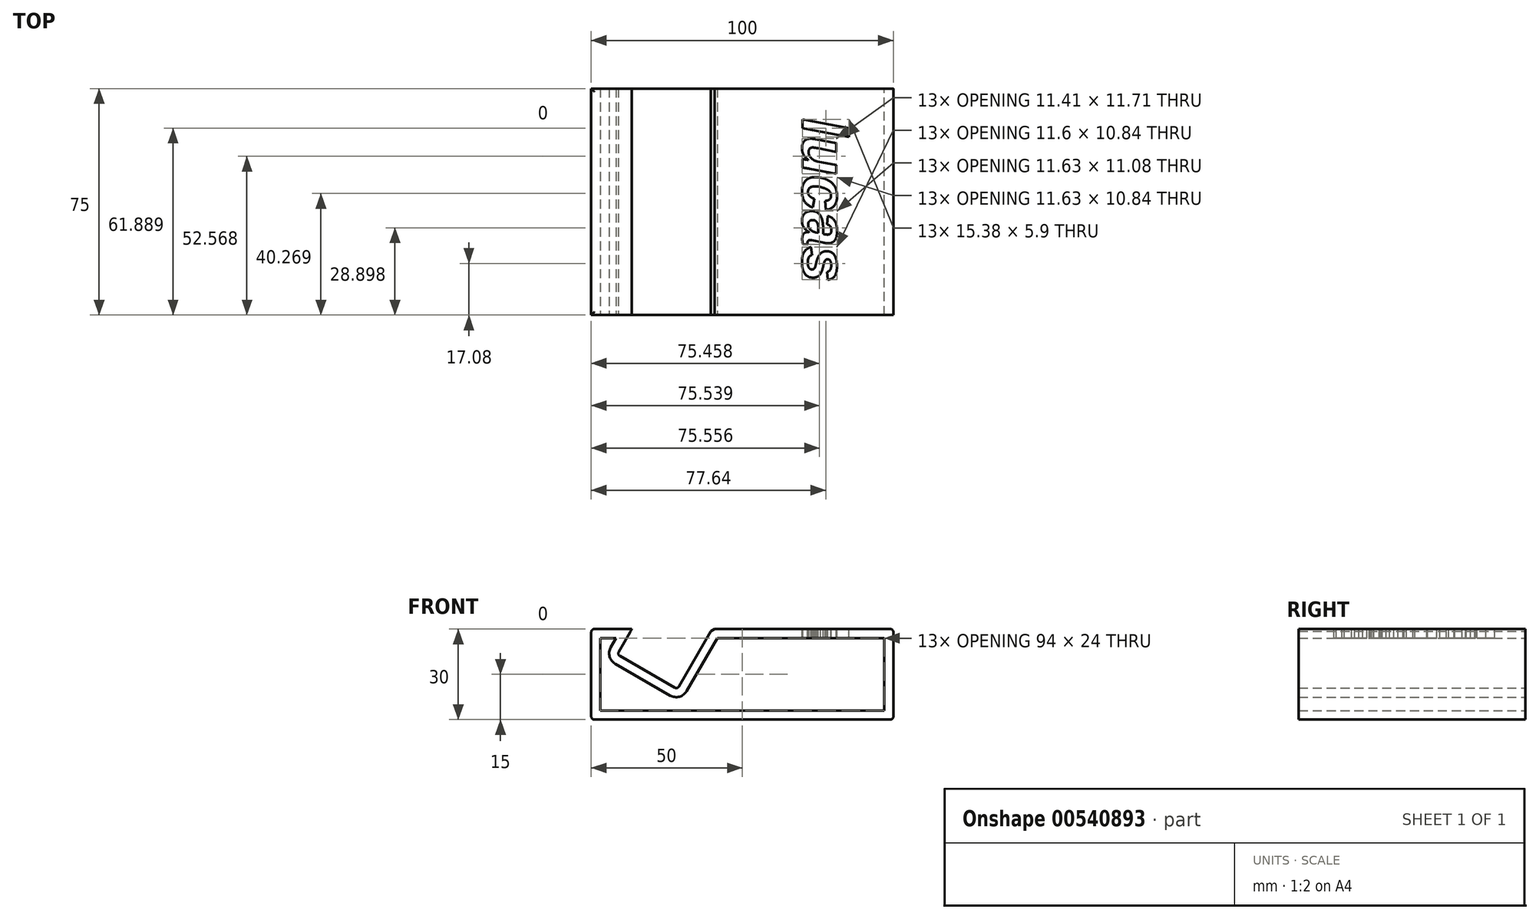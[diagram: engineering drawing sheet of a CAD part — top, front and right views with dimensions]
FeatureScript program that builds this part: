
annotation { "Feature Type Name" : "Feature", "Feature Type Description" : "" }
export const myFeature = defineFeature(function(context is Context, id is Id, definition is map)
    precondition{}
    {
        {
            var Q0;
            Q0=qCreatedBy(makeId("Top.planeOp"),FACE);
            var sketch = newSketch(context, id + "F0", { "sketchPlane" : qUnion([Q0])});
            skLineSegment(sketch, "E0.bottom", {"start": v(50, 37.5) * mm, "end": v(-50, 37.5) * mm});
            skLineSegment(sketch, "E0.top", {"start": v(50, -37.5) * mm, "end": v(-50, -37.5) * mm});
            skLineSegment(sketch, "E0.left", {"start": v(50, 37.5) * mm, "end": v(50, -37.5) * mm});
            skLineSegment(sketch, "E0.right", {"start": v(-50, 37.5) * mm, "end": v(-50, -37.5) * mm});
            skPoint(sketch, "E0.middle", {"position": v(0, 0) * mm});
            skSolve(sketch);
        }
        {
            var Q0;
            Q0=makeQuery(id+"F0.imprint","IMPRINT",FACE,{"disambiguationData":[TD([[makeQuery(id+"F0.imprint","IMPRINT",EDGE,{"derivedFrom":sQuery(id+"F0.wireOp",EDGE,"E0.bottom")}),1.0]])]});
            extrude(context, id + "F1", {"entities" : qUnion([Q0]), "depth" : 30 * mm, "offsetDistance" : 25 * mm});
        }
        {
            var Q0;
            Q0=makeQuery(id+"F1.opExtrude","SWEPT_FACE",FACE,{"disambiguationData":[OSD([sQuery(id+"F0.wireOp",EDGE,"E0.top")])]});
            var sketch = newSketch(context, id + "F2", { "sketchPlane" : qUnion([Q0])});
            skLineSegment(sketch, "E1.bottom", {"start": v(-10, 30) * mm, "end": v(-21.5, 10.08) * mm});
            skLineSegment(sketch, "E1.top", {"start": v(-29.92, 41.5) * mm, "end": v(-41.42, 21.58) * mm});
            skLineSegment(sketch, "E1.left", {"start": v(-10, 30) * mm, "end": v(-29.92, 41.5) * mm});
            skLineSegment(sketch, "E1.right", {"start": v(-21.5, 10.08) * mm, "end": v(-41.42, 21.58) * mm});
            skSolve(sketch);
        }
        {
            var Q0;
            {var subQ0=sQuery(id+"F2.wireOp",EDGE,"E1.bottom");Q0=makeQuery(id+"F2.imprint","IMPRINT",FACE,{"disambiguationData":[TD([[makeQuery(id+"F2.imprint","IMPRINT",EDGE,{"derivedFrom":subQ0}),-1.0]])]});}
            extrude(context, id + "F3", {"entities" : qUnion([Q0]), "operationType" : NewBodyOperationType.REMOVE, "oppositeDirection" : true, "depth" : 75 * mm, "offsetDistance" : 25 * mm});
        }
        {
            var Q0;
            Q0=makeQuery(id+"F3.boolean.opBoolean","COPY",EDGE,{"derivedFrom":makeQuery(id+"F3.opExtrude","SWEPT_EDGE",EDGE,{"disambiguationData":[OSD([sQuery(id+"F0.wireOp",EDGE,"E0.top"),sQuery(id+"F2.wireOp",EDGE,"E1.bottom"),sQuery(id+"F2.wireOp",EDGE,"E1.left")])]})});
            chamfer(context, id + "F4", {"entities" : qUnion([Q0]), "width" : 1.5 * mm, "tangentPropagation" : true});
        }
        {
            var Q0;
            Q0=makeQuery(id+"F3.boolean.opBoolean","COPY",EDGE,{"derivedFrom":makeQuery(id+"F3.opExtrude","SWEPT_EDGE",EDGE,{"disambiguationData":[OSD([sQuery(id+"F0.wireOp",EDGE,"E0.top"),sQuery(id+"F2.wireOp",EDGE,"E1.top")])]})});
            var Q1;
            Q1=makeQuery(id+"F1.opExtrude","CAP_EDGE",EDGE,{"disambiguationData":[OSD([sQuery(id+"F0.wireOp",EDGE,"E0.right")])],"isStart":false});
            var Q2;
            {var subQ0=sQuery(id+"F0.wireOp",EDGE,"E0.right");var subQ1=sQuery(id+"F0.wireOp",EDGE,"E0.top");Q2=makeQuery(id+"F3.boolean.opBoolean","SPLIT",EDGE,{"disambiguationData":[TD([makeQuery(id+"F1.opExtrude","SWEPT_FACE",FACE,{"disambiguationData":[OSD([subQ0])]})])],"derivedFrom":makeQuery(id+"F1.opExtrude","CAP_EDGE",EDGE,{"disambiguationData":[OSD([subQ1])],"isStart":false})});}
            var Q3;
            {var subQ0=sQuery(id+"F0.wireOp",EDGE,"E0.bottom");var subQ1=sQuery(id+"F0.wireOp",EDGE,"E0.right");Q3=makeQuery(id+"F3.boolean.opBoolean","SPLIT",EDGE,{"disambiguationData":[TD([makeQuery(id+"F1.opExtrude","SWEPT_FACE",FACE,{"disambiguationData":[OSD([subQ1])]})])],"derivedFrom":makeQuery(id+"F1.opExtrude","CAP_EDGE",EDGE,{"disambiguationData":[OSD([subQ0])],"isStart":false})});}
            var Q4;
            Q4=makeQuery(id+"F3.boolean.opBoolean","COPY",EDGE,{"derivedFrom":makeQuery(id+"F3.opExtrude","SWEPT_EDGE",EDGE,{"disambiguationData":[OSD([sQuery(id+"F2.wireOp",EDGE,"E1.top"),sQuery(id+"F2.wireOp",EDGE,"E1.right")])]})});
            var Q5;
            Q5=makeQuery(id+"F3.boolean.opBoolean","COPY",EDGE,{"derivedFrom":makeQuery(id+"F3.opExtrude","CAP_EDGE",EDGE,{"disambiguationData":[OSD([sQuery(id+"F2.wireOp",EDGE,"E1.top")])],"isStart":false})});
            var Q6;
            Q6=makeQuery(id+"F1.opExtrude","CAP_EDGE",EDGE,{"disambiguationData":[OSD([sQuery(id+"F0.wireOp",EDGE,"E0.left")])],"isStart":false});
            var Q7;
            Q7=makeQuery(id+"F1.opExtrude","CAP_EDGE",EDGE,{"disambiguationData":[OSD([sQuery(id+"F0.wireOp",EDGE,"E0.left")])],"isStart":true});
            var Q8;
            Q8=makeQuery(id+"F1.opExtrude","CAP_EDGE",EDGE,{"disambiguationData":[OSD([sQuery(id+"F0.wireOp",EDGE,"E0.right")])],"isStart":true});
            var Q9;
            Q9=makeQuery(id+"F3.boolean.opBoolean","COPY",EDGE,{"derivedFrom":makeQuery(id+"F3.opExtrude","SWEPT_EDGE",EDGE,{"disambiguationData":[OSD([sQuery(id+"F2.wireOp",EDGE,"E1.bottom"),sQuery(id+"F2.wireOp",EDGE,"E1.right")])]})});
            var Q10;
            Q10=makeQuery(id+"F3.boolean.opBoolean","COPY",EDGE,{"derivedFrom":makeQuery(id+"F3.opExtrude","CAP_EDGE",EDGE,{"disambiguationData":[OSD([sQuery(id+"F2.wireOp",EDGE,"E1.top")])],"isStart":true})});
            var Q11;
            Q11=makeQuery(id+"F3.boolean.opBoolean","COPY",EDGE,{"derivedFrom":makeQuery(id+"F3.opExtrude","CAP_EDGE",EDGE,{"disambiguationData":[OSD([sQuery(id+"F2.wireOp",EDGE,"E1.right")])],"isStart":true})});
            var Q12;
            Q12=makeQuery(id+"F3.boolean.opBoolean","COPY",EDGE,{"derivedFrom":makeQuery(id+"F3.opExtrude","CAP_EDGE",EDGE,{"disambiguationData":[OSD([sQuery(id+"F2.wireOp",EDGE,"E1.bottom")])],"isStart":true})});
            fillet(context, id + "F5", {"entities" : qUnion([Q0, Q1, Q2, Q3, Q4, Q5, Q6, Q7, Q8, Q9, Q10, Q11, Q12]), "radius" : 1 * mm, "tangentPropagation" : true, "allowEdgeOverflow" : false});
        }
        {
            var Q0;
            Q0=makeQuery(id+"F1.opExtrude","SWEPT_FACE",FACE,{"disambiguationData":[OSD([sQuery(id+"F0.wireOp",EDGE,"E0.top")])]});
            var Q1;
            Q1=makeQuery(id+"F1.opExtrude","SWEPT_FACE",FACE,{"disambiguationData":[OSD([sQuery(id+"F0.wireOp",EDGE,"E0.bottom")])]});
            shell(context, id + "F6", {"entities" : qUnion([Q0, Q1]), "thickness" : 3 * mm});
        }
        {
            var Q0;
            {var subQ0=sQuery(id+"F0.wireOp",EDGE,"E0.bottom");var subQ1=sQuery(id+"F0.wireOp",EDGE,"E0.top");var subQ2=sQuery(id+"F0.wireOp",EDGE,"E0.left");Q0=makeQuery(id+"F3.boolean.opBoolean","SPLIT",FACE,{"disambiguationData":[TD([makeQuery(id+"F1.opExtrude","SWEPT_FACE",FACE,{"disambiguationData":[OSD([subQ2])]})])],"derivedFrom":makeQuery(id+"F1.opExtrude","CAP_FACE",FACE,{"disambiguationData":[OSD([subQ0,subQ1,subQ2,sQuery(id+"F0.wireOp",EDGE,"E0.right")])],"isStart":false})});}
            var sketch = newSketch(context, id + "F7", { "sketchPlane" : qUnion([Q0])});
            skText(sketch, "E2", { "text": "lucas", "fontName": "Arimo-BoldItalic.ttf"});
            const initialGuessF7  = {"E2": [0.01995, 0.0277, 0, -1, 0.01528]};
            skSetInitialGuess(sketch, initialGuessF7);
            skSolve(sketch);
        }
        {
            var Q0;
            Q0 = qSketchRegion(id + "F7", true);
            extrude(context, id + "F8", {"entities" : qUnion([Q0]), "operationType" : NewBodyOperationType.REMOVE, "oppositeDirection" : true, "depth" : 2 * mm, "offsetDistance" : 25 * mm});
        }
        {
            var Q0;
            Q0 = qSketchRegion(id + "F7", true);
            extrude(context, id + "F9", {"entities" : qUnion([Q0]), "operationType" : NewBodyOperationType.REMOVE, "oppositeDirection" : true, "depth" : 25 * mm, "offsetDistance" : 25 * mm});
        }
    });
